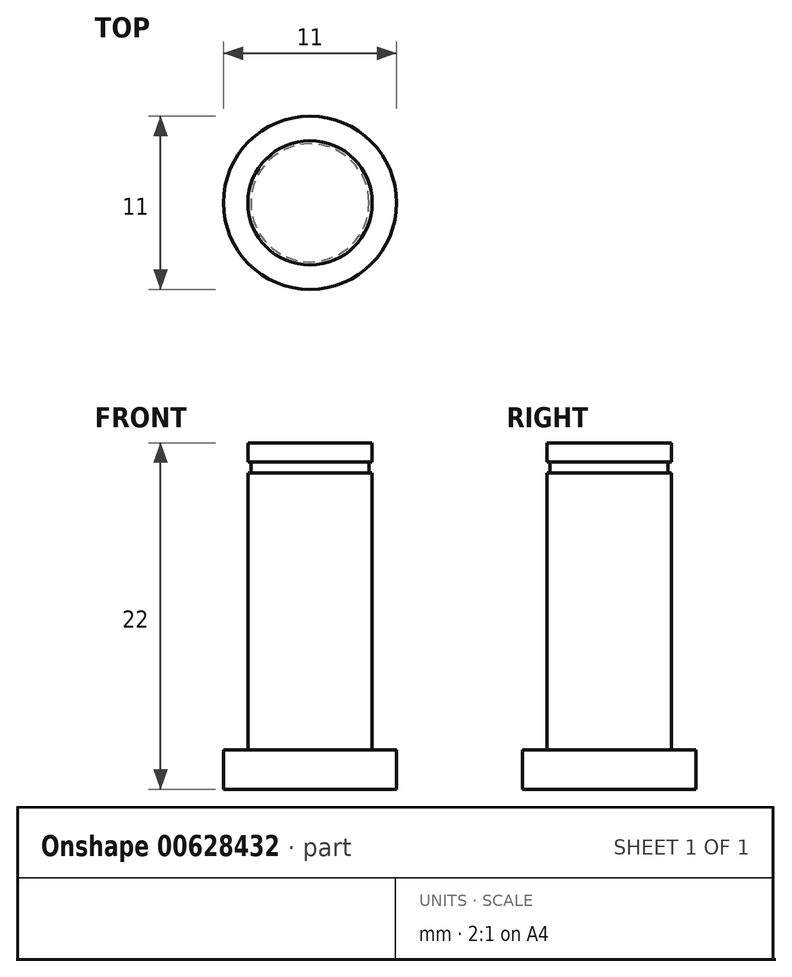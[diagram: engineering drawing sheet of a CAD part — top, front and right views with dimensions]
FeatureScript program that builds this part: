
annotation { "Feature Type Name" : "Feature", "Feature Type Description" : "" }
export const myFeature = defineFeature(function(context is Context, id is Id, definition is map)
    precondition{}
    {
        {
            var Q0;
            Q0=qCreatedBy(makeId("Top.planeOp"),FACE);
            var sketch = newSketch(context, id + "F0", { "sketchPlane" : qUnion([Q0])});
            skCircle(sketch, "E0", {"center": v(0, 0) * mm, "radius": 3.95 * mm});
            skSolve(sketch);
        }
        {
            var Q0;
            Q0 = qSketchRegion(id + "F0", true);
            extrude(context, id + "F1", {"entities" : qUnion([Q0]), "depth" : 22 * mm, "offsetDistance" : 25 * mm});
        }
        {
            var Q0;
            Q0=qCreatedBy(makeId("Top.planeOp"),FACE);
            var sketch = newSketch(context, id + "F2", { "sketchPlane" : qUnion([Q0])});
            skCircle(sketch, "E1", {"center": v(0, 0) * mm, "radius": 5.5 * mm});
            skSolve(sketch);
        }
        {
            var Q0;
            Q0=makeQuery(id+"F2.imprint","IMPRINT",FACE,{"disambiguationData":[TD([[makeQuery(id+"F2.imprint","IMPRINT",EDGE,{"derivedFrom":sQuery(id+"F2.wireOp",EDGE,"E1")}),1.0]])]});
            extrude(context, id + "F3", {"entities" : qUnion([Q0]), "operationType" : NewBodyOperationType.ADD, "depth" : 2.5 * mm, "offsetDistance" : 25 * mm});
        }
        {
            var Q0;
            Q0=qCreatedBy(makeId("Top.planeOp"),FACE);
            var sketch = newSketch(context, id + "F4", { "sketchPlane" : qUnion([Q0])});
            skCircle(sketch, "E2", {"center": v(0, 0) * mm, "radius": 3.75 * mm});
            skCircle(sketch, "E3", {"center": v(0, 0) * mm, "radius": 7.44 * mm});
            skSolve(sketch);
        }
        {
            var Q0;
            Q0 = qSketchRegion(id + "F4", true);
            extrude(context, id + "F5", {"entities" : qUnion([Q0]), "depth" : .7 * mm, "offsetDistance" : 25 * mm});
        }
        {
            var Q0;
            Q0=makeQuery(id+"F5.opExtrude","SWEPT_BODY",BODY,{"disambiguationData":[OSD([sQuery(id+"F4.wireOp",EDGE,"E2")])]});
            transform(context, id + "F6", {"entities" : qUnion([Q0]), "transformType" : TransformType.TRANSLATION_3D, "dx" : 0 * mm, "dy" : 0 * mm, "dz" : 20.1 * mm, "makeCopy" : false});
        }
        {
            var Q0;
            Q0=makeQuery(id+"F5.opExtrude","SWEPT_BODY",BODY,{"disambiguationData":[OSD([sQuery(id+"F4.wireOp",EDGE,"E2"),sQuery(id+"F4.wireOp",EDGE,"E3")])]});
            var Q1;
            Q1=makeQuery(id+"F1.opExtrude","SWEPT_BODY",BODY,{"disambiguationData":[OSD([sQuery(id+"F0.wireOp",EDGE,"E0")])]});
            booleanBodies(context, id + "F7", {"operationType" : BooleanOperationType.SUBTRACTION, "tools" : qUnion([Q0]), "targets" : qUnion([Q1])});
        }
    });
